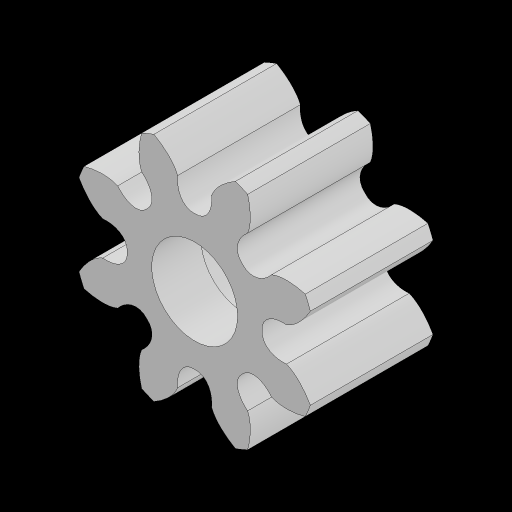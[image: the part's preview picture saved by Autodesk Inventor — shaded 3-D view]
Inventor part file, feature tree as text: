
AUTODESK INVENTOR PART (.ipt)
format: ipt  version: 2023.2 (Build 272271030, 271C)  size: 245,248 bytes
history: native  units: mm
features: extrude x4, sketch x3, pattern_circular x1, chamfer x1, projected_geometry x1
ambient origin geometry x8: Origin, YZ Plane, XZ Plane, XY Plane, X Axis, Y Axis, Z Axis, Center Point
bodies: Solid1 (feature_tree)
feature tree (10):
  sketch  "Sketch1"  dims[d0=5.0mm d1=0.0mm d2=4.0mm]
  extrude  "Extrusion1"  Depth=4.0mm
  sketch  "Sketch2"  dims[d3=0.0mm d4=0.0mm d5=80.0mm d6=360.0deg]
  extrude  "Extrusion2"  Depth=80.0mm TaperAngle=360.0deg
  pattern_circular  "Circular Pattern1"  [2 undecoded]
  extrude  "Extrusion3"  Depth=2.0mm TaperAngle=0.0deg
  extrude  "Extrusion4"  Depth=2.0mm TaperAngle=45.0deg
  chamfer  "Chamfer1"  [1 undecoded]
  sketch  "Sketch3"  dims[d8=0.0mm d9=0.0mm d10=3.5mm d11=2.0mm d12=0.0mm d13=0.5mm d14=2.0mm d15=45.0deg]
  projected_geometry  "Projected Loop1"
note: 3 required parameter values undecoded (feature->parameter linkage not recoverable at this tier; creation-order binding heuristic only, values carry confidence <= 0.55)
